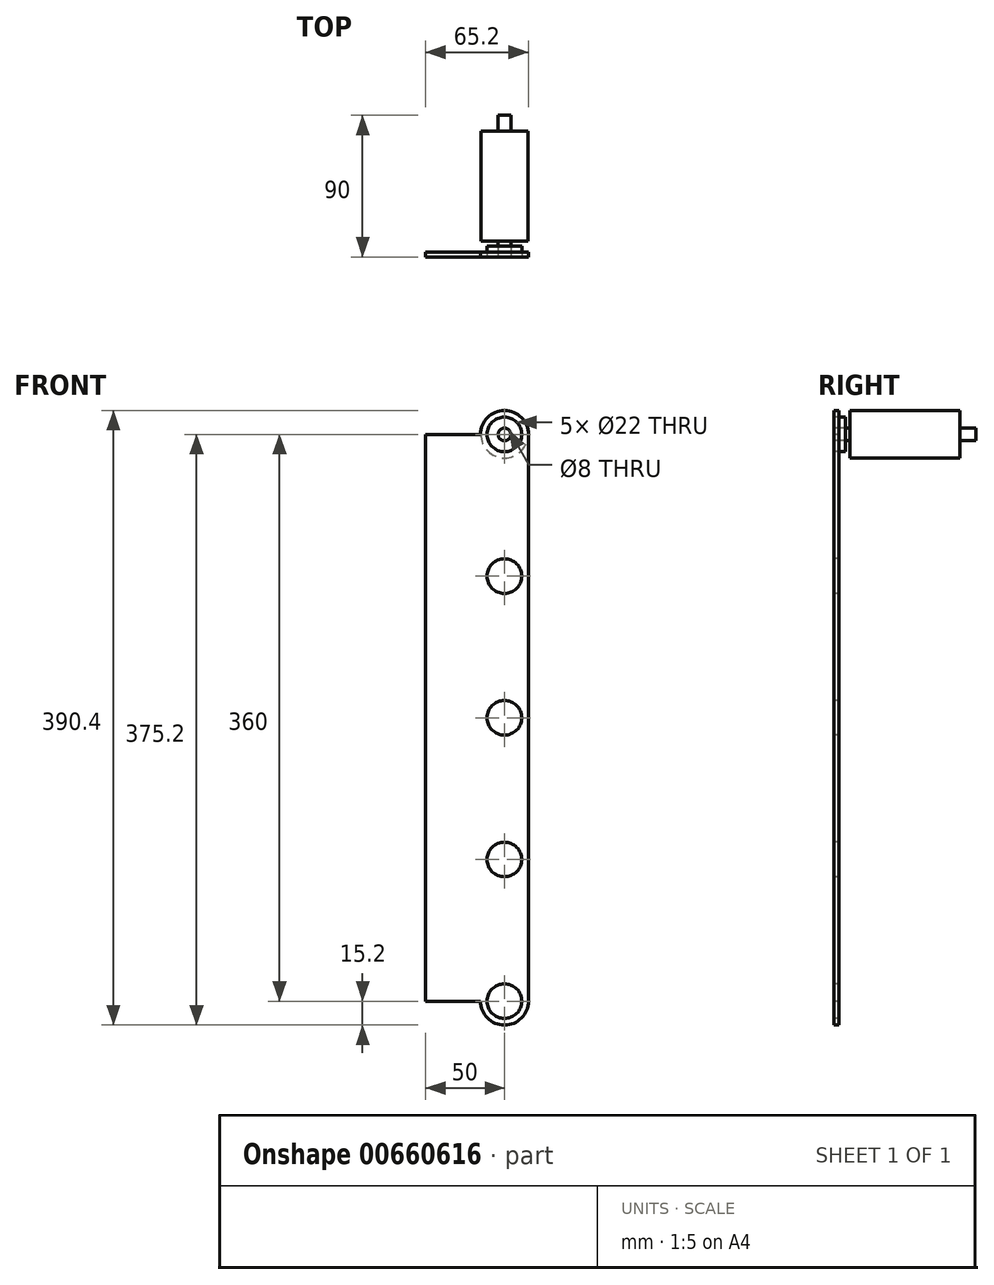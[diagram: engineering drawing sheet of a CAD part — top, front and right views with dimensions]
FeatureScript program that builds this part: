
annotation { "Feature Type Name" : "Feature", "Feature Type Description" : "" }
export const myFeature = defineFeature(function(context is Context, id is Id, definition is map)
    precondition{}
    {
        {
            var Q0;
            Q0=qCreatedBy(makeId("Front.planeOp"),FACE);
            var sketch = newSketch(context, id + "F0", { "sketchPlane" : qUnion([Q0])});
            skCircle(sketch, "E0", {"center": v(0, 0) * mm, "radius": 4 * mm});
            skSolve(sketch);
        }
        {
            var Q0;
            Q0 = qSketchRegion(id + "F0", true);
            extrude(context, id + "F1", {"entities" : qUnion([Q0]), "endBound" : BoundingType.SYMMETRIC, "depth" : 90 * mm, "offsetDistance" : 25 * mm});
        }
        {
            var Q0;
            Q0=makeQuery(id+"F1.opExtrude","CAP_FACE",FACE,{"disambiguationData":[OSD([sQuery(id+"F0.wireOp",EDGE,"E0")])],"isStart":false});
            var sketch = newSketch(context, id + "F2", { "sketchPlane" : qUnion([Q0])});
            skCircle(sketch, "E1", {"center": v(0, 0) * mm, "radius": 15 * mm});
            skSolve(sketch);
        }
        {
            var Q0;
            Q0 = qSketchRegion(id + "F2", true);
            extrude(context, id + "F3", {"entities" : qUnion([Q0]), "operationType" : NewBodyOperationType.ADD, "oppositeDirection" : true, "depth" : 80 * mm, "offsetDistance" : 25 * mm, "hasSecondDirection" : true, "secondDirectionOppositeDirection" : true, "secondDirectionDepth" : 10 * mm});
        }
        {
            var Q0;
            Q0=makeQuery(id+"F1.opExtrude","CAP_FACE",FACE,{"disambiguationData":[OSD([sQuery(id+"F0.wireOp",EDGE,"E0")])],"isStart":false});
            var sketch = newSketch(context, id + "F4", { "sketchPlane" : qUnion([Q0])});
            skCircle(sketch, "E2", {"center": v(0, 0) * mm, "radius": 4 * mm});
            skCircle(sketch, "E3", {"center": v(0, 0) * mm, "radius": 11 * mm});
            skSolve(sketch);
        }
        {
            var Q0;
            Q0 = qSketchRegion(id + "F4", true);
            extrude(context, id + "F5", {"entities" : qUnion([Q0]), "oppositeDirection" : true, "depth" : 7 * mm, "offsetDistance" : 25 * mm});
        }
        {
            var Q0;
            Q0=makeQuery(id+"F5.opExtrude","CAP_FACE",FACE,{"disambiguationData":[OSD([sQuery(id+"F4.wireOp",EDGE,"E2"),sQuery(id+"F4.wireOp",EDGE,"E3")])],"isStart":true});
            var sketch = newSketch(context, id + "F6", { "sketchPlane" : qUnion([Q0])});
            skLineSegment(sketch, "E4.bottom", {"start": v(30, 28.95) * mm, "end": v(-50, 28.95) * mm});
            skLineSegment(sketch, "E4.top", {"start": v(30, -381.05) * mm, "end": v(-50, -381.05) * mm});
            skLineSegment(sketch, "E4.left", {"start": v(30, 28.95) * mm, "end": v(30, -381.05) * mm});
            skLineSegment(sketch, "E4.right", {"start": v(-50, 28.95) * mm, "end": v(-50, -381.05) * mm});
            skCircle(sketch, "E5", {"center": v(0, 0) * mm, "radius": 11 * mm});
            skCircle(sketch, "E6.0.1.0", {"center": v(0, -90) * mm, "radius": 11 * mm});
            skCircle(sketch, "E6.0.2.0", {"center": v(0, -180) * mm, "radius": 11 * mm});
            skCircle(sketch, "E6.0.3.0", {"center": v(0, -270) * mm, "radius": 11 * mm});
            skCircle(sketch, "E6.0.4.0", {"center": v(0, -360) * mm, "radius": 11 * mm});
            skLineSegment(sketch, "E6.direction1", {"start": v(0, 0) * mm, "end": v(25, 0) * mm, "construction": true});
            skLineSegment(sketch, "E6.direction2", {"start": v(0, 0) * mm, "end": v(0, -90) * mm, "construction": true});
            skSolve(sketch);
        }
        {
            var Q0;
            Q0 = qSketchRegion(id + "F6", true);
            extrude(context, id + "F7", {"entities" : qUnion([Q0]), "oppositeDirection" : true, "depth" : 3 * mm, "offsetDistance" : 25 * mm});
        }
        {
            var Q0;
            Q0=makeQuery(id+"F7.opExtrude","CAP_FACE",FACE,{"disambiguationData":[OSD([sQuery(id+"F6.wireOp",EDGE,"E4.bottom"),sQuery(id+"F6.wireOp",EDGE,"E4.top"),sQuery(id+"F6.wireOp",EDGE,"E4.left"),sQuery(id+"F6.wireOp",EDGE,"E4.right"),sQuery(id+"F6.wireOp",EDGE,"E5"),sQuery(id+"F6.wireOp",EDGE,"E6.0.1.0"),sQuery(id+"F6.wireOp",EDGE,"E6.0.2.0"),sQuery(id+"F6.wireOp",EDGE,"E6.0.3.0"),sQuery(id+"F6.wireOp",EDGE,"E6.0.4.0")])],"isStart":true});
            var sketch = newSketch(context, id + "F8", { "sketchPlane" : qUnion([Q0])});
            skLineSegment(sketch, "E7", {"start": v(15.2, 0) * mm, "end": v(30, 0) * mm});
            skLineSegment(sketch, "E8", {"start": v(30, 0) * mm, "end": v(30, 46.04) * mm});
            skLineSegment(sketch, "E9", {"start": v(30, 46.04) * mm, "end": v(-84.69, 56.97) * mm});
            skLineSegment(sketch, "E10", {"start": v(-84.69, 56.97) * mm, "end": v(-90.12, 0) * mm});
            skLineSegment(sketch, "E11", {"start": v(-90.12, 0) * mm, "end": v(-15.2, 0) * mm});
            skLineSegment(sketch, "E12", {"start": v(15.2, -360) * mm, "end": v(30, -360) * mm});
            skLineSegment(sketch, "E13", {"start": v(30, -360) * mm, "end": v(30, -381.05) * mm});
            skLineSegment(sketch, "E14", {"start": v(30, -381.05) * mm, "end": v(-50, -381.05) * mm});
            skLineSegment(sketch, "E15", {"start": v(-50, -381.05) * mm, "end": v(-50, -360) * mm});
            skLineSegment(sketch, "E16", {"start": v(-50, -360) * mm, "end": v(-15.2, -360) * mm});
            skArc(sketch, "E17", {"start": v(-15.2, -360) * mm, "mid": v(0, -375.2) * mm, "end": v(15.2, -360) * mm});
            skArc(sketch, "E18", {"start": v(15.2, 0) * mm, "mid": v(0, 15.2) * mm, "end": v(-15.2, 0) * mm});
            skLineSegment(sketch, "E19", {"start": v(30, 0) * mm, "end": v(30, -360) * mm});
            skLineSegment(sketch, "E20", {"start": v(15.2, -360) * mm, "end": v(15.2, 0) * mm});
            skSolve(sketch);
        }
        {
            var Q0;
            Q0 = qSketchRegion(id + "F8", true);
            extrude(context, id + "F9", {"entities" : qUnion([Q0]), "operationType" : NewBodyOperationType.REMOVE, "oppositeDirection" : true, "depth" : 25 * mm, "offsetDistance" : 25 * mm});
        }
    });
